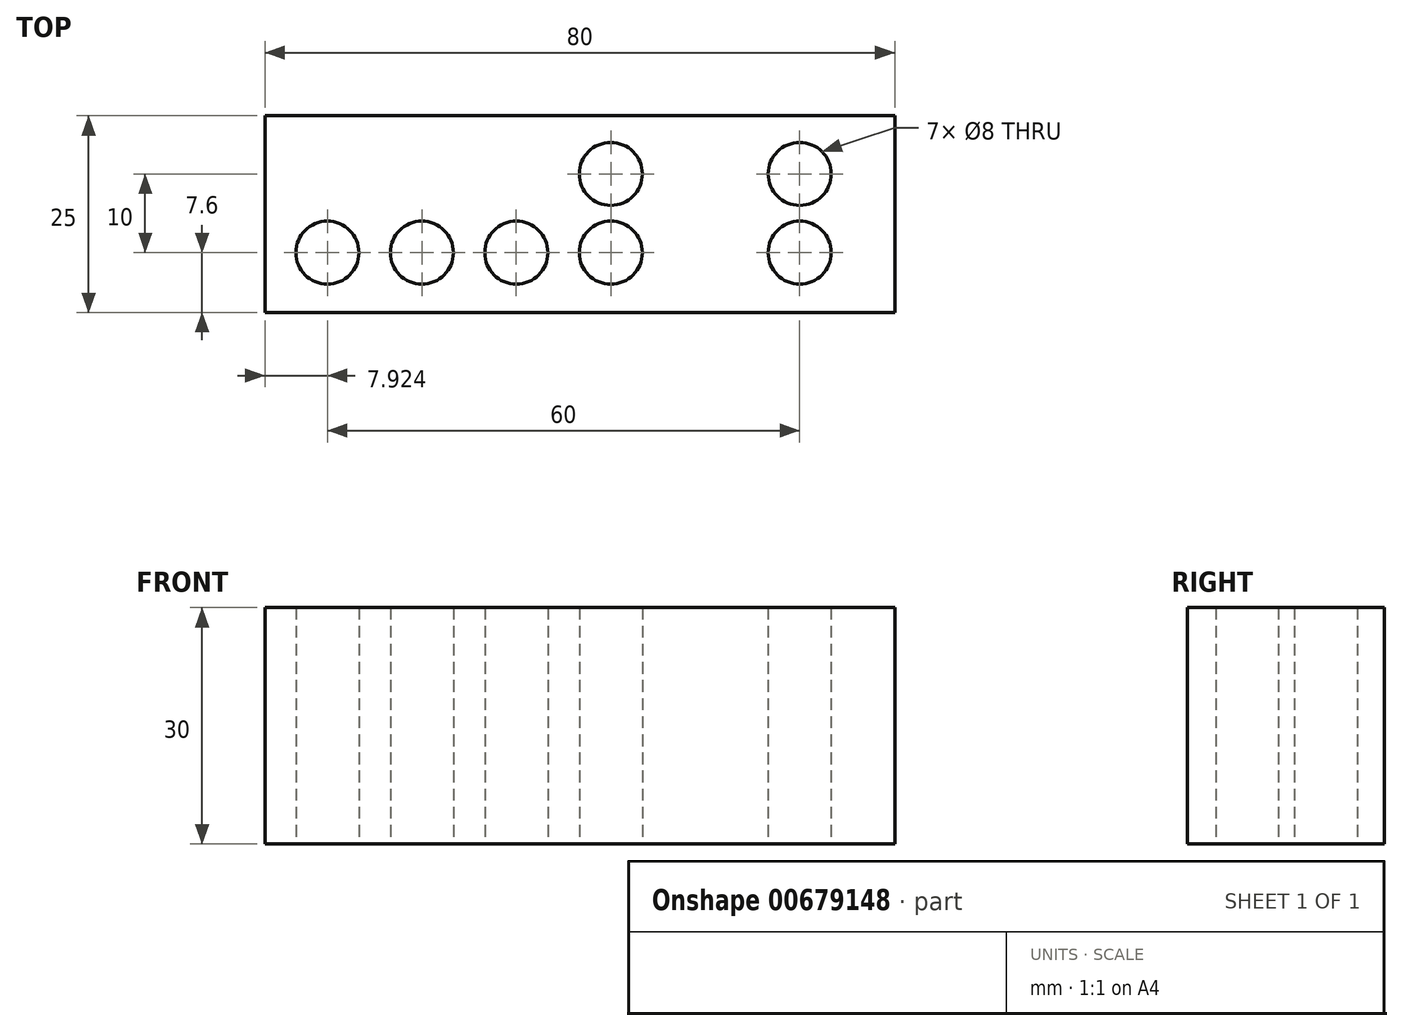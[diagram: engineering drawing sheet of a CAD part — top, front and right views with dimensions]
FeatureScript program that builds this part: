
annotation { "Feature Type Name" : "Feature", "Feature Type Description" : "" }
export const myFeature = defineFeature(function(context is Context, id is Id, definition is map)
    precondition{}
    {
        {
            var Q0;
            Q0=qCreatedBy(makeId("Front.planeOp"),FACE);
            var sketch = newSketch(context, id + "F0", { "sketchPlane" : qUnion([Q0])});
            skLineSegment(sketch, "E0.bottom", {"start": v(40, 15) * mm, "end": v(-40, 15) * mm});
            skLineSegment(sketch, "E0.top", {"start": v(40, -15) * mm, "end": v(-40, -15) * mm});
            skLineSegment(sketch, "E0.left", {"start": v(40, 15) * mm, "end": v(40, -15) * mm});
            skLineSegment(sketch, "E0.right", {"start": v(-40, 15) * mm, "end": v(-40, -15) * mm});
            skPoint(sketch, "E0.middle", {"position": v(0, 0) * mm});
            skSolve(sketch);
        }
        {
            var Q0;
            Q0 = qSketchRegion(id + "F0", true);
            extrude(context, id + "F1", {"entities" : qUnion([Q0]), "depth" : 25 * mm, "offsetDistance" : 25 * mm});
        }
        {
            var Q0;
            Q0=makeQuery(id+"F1.opExtrude","SWEPT_FACE",FACE,{"disambiguationData":[OSD([sQuery(id+"F0.wireOp",EDGE,"E0.top")])]});
            var sketch = newSketch(context, id + "F2", { "sketchPlane" : qUnion([Q0])});
            skCircle(sketch, "E1", {"center": v(-32.08, 7.4) * mm, "radius": 3.78 * mm});
            skCircle(sketch, "E2.0.1.0", {"center": v(-32.08, 17.4) * mm, "radius": 3.78 * mm});
            skCircle(sketch, "E2.1.0.0", {"center": v(-20.08, 7.4) * mm, "radius": 3.78 * mm});
            skCircle(sketch, "E2.1.1.0", {"center": v(-20.08, 17.4) * mm, "radius": 3.78 * mm});
            skCircle(sketch, "E2.2.0.0", {"center": v(-8.08, 7.4) * mm, "radius": 3.78 * mm});
            skCircle(sketch, "E2.2.1.0", {"center": v(-8.08, 17.4) * mm, "radius": 3.78 * mm});
            skCircle(sketch, "E2.3.0.0", {"center": v(3.92, 7.4) * mm, "radius": 3.78 * mm});
            skCircle(sketch, "E2.3.1.0", {"center": v(3.92, 17.4) * mm, "radius": 3.78 * mm});
            skCircle(sketch, "E2.4.0.0", {"center": v(15.92, 7.4) * mm, "radius": 3.78 * mm});
            skCircle(sketch, "E2.4.1.0", {"center": v(15.92, 17.4) * mm, "radius": 3.78 * mm});
            skCircle(sketch, "E2.5.0.0", {"center": v(27.92, 7.4) * mm, "radius": 3.78 * mm});
            skCircle(sketch, "E2.5.1.0", {"center": v(27.92, 17.4) * mm, "radius": 3.78 * mm});
            skLineSegment(sketch, "E2.direction1", {"start": v(-32.08, 7.4) * mm, "end": v(-20.08, 7.4) * mm, "construction": true});
            skLineSegment(sketch, "E2.direction2", {"start": v(-32.08, 7.4) * mm, "end": v(-32.08, 17.4) * mm, "construction": true});
            skSolve(sketch);
        }
        {
            var Q0;
            Q0=sQuery(id+"F2.wireOp",VERTEX,"E2.direction2.end");
            var Q1;
            Q1=sQuery(id+"F2.wireOp",VERTEX,"E2.1.1.0.center");
            var Q2;
            Q2=sQuery(id+"F2.wireOp",VERTEX,"E2.2.1.0.center");
            var Q3;
            Q3=sQuery(id+"F2.wireOp",VERTEX,"E2.3.1.0.center");
            var Q4;
            Q4=sQuery(id+"F2.wireOp",VERTEX,"E2.4.1.0.center");
            var Q5;
            Q5=sQuery(id+"F2.wireOp",VERTEX,"E2.5.1.0.center");
            var Q6;
            Q6=sQuery(id+"F2.wireOp",VERTEX,"E2.5.0.0.center");
            var Q7;
            Q7=sQuery(id+"F2.wireOp",VERTEX,"E2.4.0.0.center");
            var Q8;
            Q8=sQuery(id+"F2.wireOp",VERTEX,"E2.3.0.0.center");
            var Q9;
            Q9=sQuery(id+"F2.wireOp",VERTEX,"E2.1.0.0.center");
            var Q10;
            Q10=sQuery(id+"F2.wireOp",VERTEX,"E2.direction1.start");
            var Q11;
            Q11=sQuery(id+"F2.wireOp",VERTEX,"E2.2.0.0.center");
            var Q12;
            Q12=makeQuery(id+"F1.opExtrude","SWEPT_BODY",BODY,{"disambiguationData":[OSD([sQuery(id+"F0.wireOp",EDGE,"E0.bottom"),sQuery(id+"F0.wireOp",EDGE,"E0.top"),sQuery(id+"F0.wireOp",EDGE,"E0.left"),sQuery(id+"F0.wireOp",EDGE,"E0.right")])]});
            hole(context, id + "F3", {"style" : HoleStyle.SIMPLE, "endStyle" : HoleEndStyle.THROUGH, "holeDiameter" : 8 * mm, "majorDiameter" : 5 * mm, "isTappedThrough" : true, "tappedDepth" : 12 * mm, "tapClearance" : 3, "locations" : qUnion([Q0, Q1, Q2, Q3, Q4, Q5, Q6, Q7, Q8, Q9, Q10, Q11]), "scope" : qUnion([Q12])});
        }
    });
